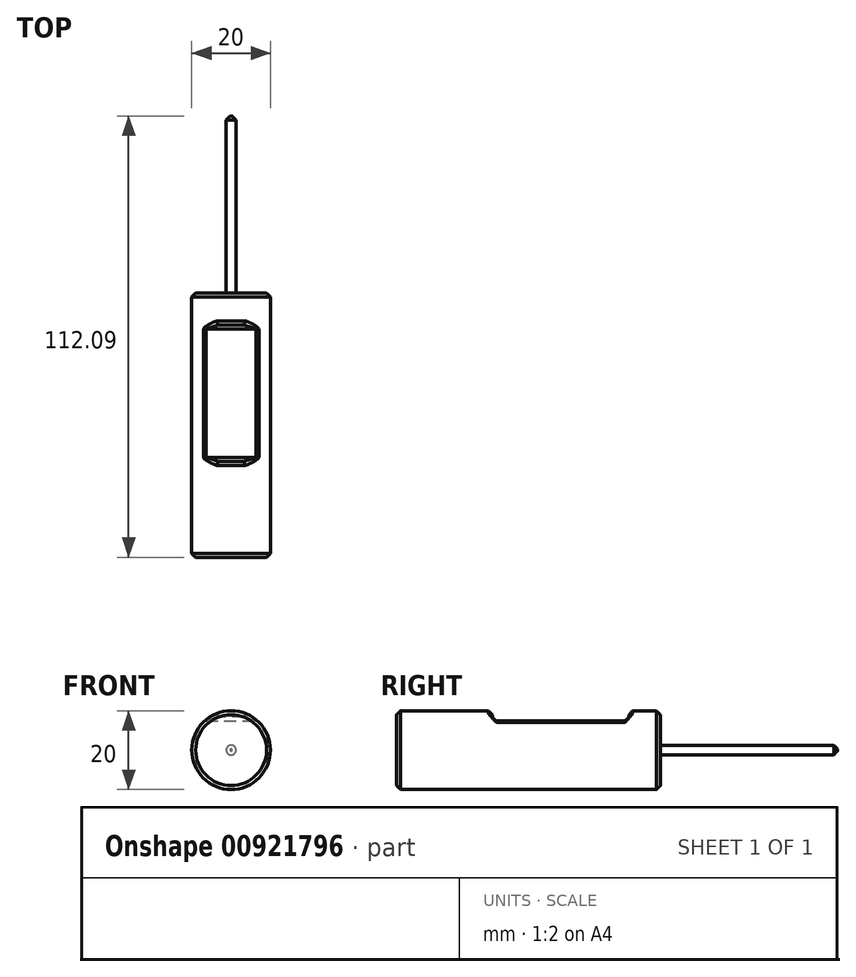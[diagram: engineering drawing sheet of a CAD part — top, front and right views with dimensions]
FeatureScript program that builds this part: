
annotation { "Feature Type Name" : "Feature", "Feature Type Description" : "" }
export const myFeature = defineFeature(function(context is Context, id is Id, definition is map)
    precondition{}
    {
        {
            var Q0;
            Q0=qCreatedBy(makeId("Right.planeOp"),FACE);
            var sketch = newSketch(context, id + "F0", { "sketchPlane" : qUnion([Q0])});
            skLineSegment(sketch, "E0", {"start": v(-67.1, 0) * mm, "end": v(-67.1, 10) * mm});
            skLineSegment(sketch, "E1", {"start": v(-67.1, 10) * mm, "end": v(0, 10) * mm});
            skLineSegment(sketch, "E2", {"start": v(0, 10) * mm, "end": v(0, 1.25) * mm});
            skLineSegment(sketch, "E3", {"start": v(0, 1.25) * mm, "end": v(45, 1.25) * mm});
            skLineSegment(sketch, "E4", {"start": v(45, 1.25) * mm, "end": v(45, 0) * mm});
            skLineSegment(sketch, "E5", {"start": v(45, 0) * mm, "end": v(-67.1, 0) * mm});
            skSolve(sketch);
        }
        {
            var Q0;
            Q0=makeQuery(id+"F0.imprint","IMPRINT",FACE,{"disambiguationData":[TD([[makeQuery(id+"F0.imprint","IMPRINT",EDGE,{"derivedFrom":sQuery(id+"F0.wireOp",EDGE,"E0")}),-1.0]])]});
            var Q1;
            Q1=sQuery(id+"F0.wireOp",EDGE,"E5");
            revolve(context, id + "F1", {"surfaceOperationType" : NewSurfaceOperationType.NEW, "entities" : qUnion([Q0]), "axis" : qUnion([Q1]), "revolveType" : RevolveType.FULL});
        }
        {
            var Q0;
            Q0=makeQuery(id+"F1.opRevolve","SWEPT_EDGE",EDGE,{"disambiguationData":[OSD([sQuery(id+"F0.wireOp",EDGE,"E0"),sQuery(id+"F0.wireOp",EDGE,"E1")])]});
            var Q1;
            Q1=makeQuery(id+"F1.opRevolve","SWEPT_EDGE",EDGE,{"disambiguationData":[OSD([sQuery(id+"F0.wireOp",EDGE,"E1"),sQuery(id+"F0.wireOp",EDGE,"E2")])]});
            chamfer(context, id + "F2", {"entities" : qUnion([Q0, Q1]), "width" : 1 * mm, "tangentPropagation" : true});
        }
        {
            var Q0;
            Q0=qCreatedBy(makeId("Right.planeOp"),FACE);
            var sketch = newSketch(context, id + "F3", { "sketchPlane" : qUnion([Q0])});
            skLineSegment(sketch, "E6.bottom", {"start": v(-42.72, 22.08) * mm, "end": v(-8.08, 22.08) * mm});
            skLineSegment(sketch, "E6.top", {"start": v(-42.72, 7.38) * mm, "end": v(-8.08, 7.38) * mm});
            skLineSegment(sketch, "E6.left", {"start": v(-42.72, 22.08) * mm, "end": v(-42.72, 7.38) * mm});
            skLineSegment(sketch, "E6.right", {"start": v(-8.08, 22.08) * mm, "end": v(-8.08, 7.38) * mm});
            skSolve(sketch);
        }
        {
            var Q0;
            Q0=makeQuery(id+"F3.imprint","IMPRINT",FACE,{"disambiguationData":[TD([[makeQuery(id+"F3.imprint","IMPRINT",EDGE,{"derivedFrom":sQuery(id+"F3.wireOp",EDGE,"E6.bottom")}),-1.0]])]});
            extrude(context, id + "F4", {"entities" : qUnion([Q0]), "operationType" : NewBodyOperationType.REMOVE, "endBound" : BoundingType.SYMMETRIC, "oppositeDirection" : true, "depth" : 25 * mm, "offsetDistance" : 25 * mm});
        }
        {
            var Q0;
            Q0=makeQuery(id+"F4.boolean.opBoolean","COPY",FACE,{"derivedFrom":makeQuery(id+"F4.opExtrude","SWEPT_FACE",FACE,{"disambiguationData":[OSD([sQuery(id+"F3.wireOp",EDGE,"E6.top")])]})});
            chamfer(context, id + "F5", {"entities" : qUnion([Q0]), "width" : 1 * mm, "tangentPropagation" : true});
        }
        {
            var Q0;
            Q0=makeQuery(id+"F1.opRevolve","SWEPT_EDGE",EDGE,{"disambiguationData":[OSD([sQuery(id+"F0.wireOp",EDGE,"E3"),sQuery(id+"F0.wireOp",EDGE,"E4")])]});
            chamfer(context, id + "F6", {"entities" : qUnion([Q0]), "width" : 1 * mm, "tangentPropagation" : true});
        }
    });
